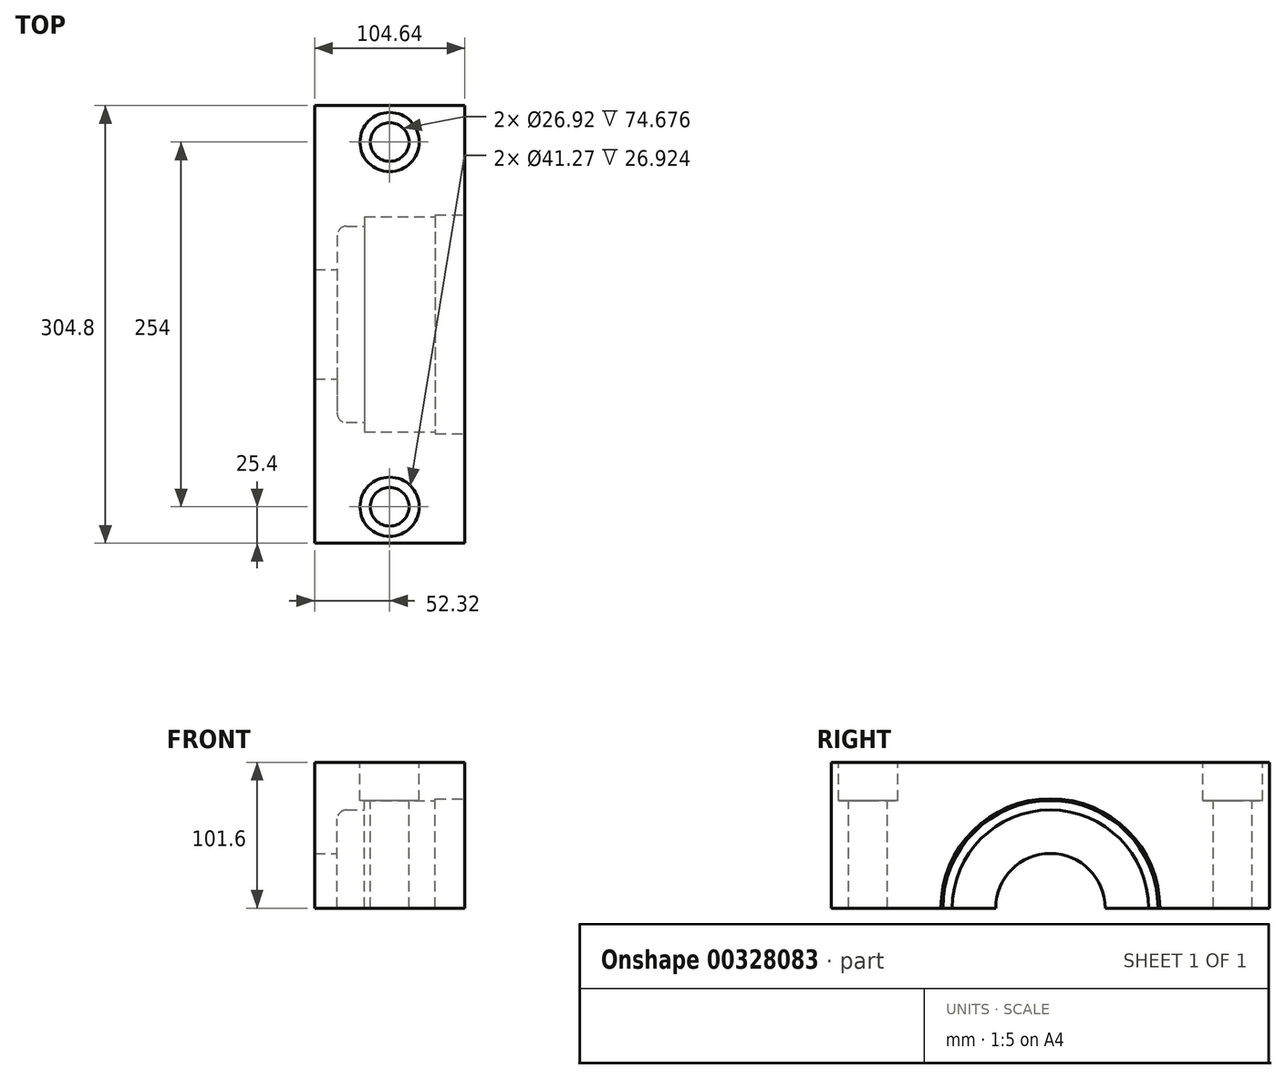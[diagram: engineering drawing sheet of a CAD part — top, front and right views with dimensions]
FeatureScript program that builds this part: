
annotation { "Feature Type Name" : "Feature", "Feature Type Description" : "" }
export const myFeature = defineFeature(function(context is Context, id is Id, definition is map)
    precondition{}
    {
        {
            var Q0;
            Q0=qCreatedBy(makeId("Right.planeOp"),FACE);
            var sketch = newSketch(context, id + "F0", { "sketchPlane" : qUnion([Q0])});
            skLineSegment(sketch, "E0.bottom", {"start": v(0, 0) * mm, "end": v(-152.4, 0) * mm});
            skLineSegment(sketch, "E0.top", {"start": v(0, 101.6) * mm, "end": v(-152.4, 101.6) * mm});
            skLineSegment(sketch, "E0.right", {"start": v(-152.4, 0) * mm, "end": v(-152.4, 101.6) * mm});
            skLineSegment(sketch, "E1.MirrorCS", {"start": v(0, 101.6) * mm, "end": v(152.4, 101.6) * mm});
            skLineSegment(sketch, "E2.MirrorCS", {"start": v(0, 0) * mm, "end": v(152.4, 0) * mm});
            skLineSegment(sketch, "E3.MirrorCS", {"start": v(152.4, 0) * mm, "end": v(152.4, 101.6) * mm});
            skSolve(sketch);
        }
        {
            var Q0;
            Q0 = qSketchRegion(id + "F0", true);
            extrude(context, id + "F1", {"entities" : qUnion([Q0]), "endBound" : BoundingType.SYMMETRIC, "depth" : 104.65 * mm});
        }
        {
            var Q0;
            Q0=makeQuery(id+"F1.opExtrude","CAP_FACE",FACE,{"disambiguationData":[OSD([sQuery(id+"F0.wireOp",EDGE,"E0.bottom"),sQuery(id+"F0.wireOp",EDGE,"E0.top"),sQuery(id+"F0.wireOp",EDGE,"E0.right"),sQuery(id+"F0.wireOp",EDGE,"E1.MirrorCS"),sQuery(id+"F0.wireOp",EDGE,"E2.MirrorCS"),sQuery(id+"F0.wireOp",EDGE,"E3.MirrorCS")])],"isStart":false});
            var sketch = newSketch(context, id + "F2", { "sketchPlane" : qUnion([Q0])});
            skCircle(sketch, "E4", {"center": v(0, 0) * mm, "radius": 38.1 * mm});
            skSolve(sketch);
        }
        {
            var Q0;
            Q0 = qSketchRegion(id + "F2", true);
            extrude(context, id + "F3", {"entities" : qUnion([Q0]), "operationType" : NewBodyOperationType.REMOVE, "endBound" : BoundingType.THROUGH_ALL, "oppositeDirection" : true, "depth" : 25.4 * mm});
        }
        {
            var Q0;
            Q0=makeQuery(id+"F1.opExtrude","CAP_FACE",FACE,{"disambiguationData":[OSD([sQuery(id+"F0.wireOp",EDGE,"E0.bottom"),sQuery(id+"F0.wireOp",EDGE,"E0.top"),sQuery(id+"F0.wireOp",EDGE,"E0.right"),sQuery(id+"F0.wireOp",EDGE,"E1.MirrorCS"),sQuery(id+"F0.wireOp",EDGE,"E2.MirrorCS"),sQuery(id+"F0.wireOp",EDGE,"E3.MirrorCS")])],"isStart":false});
            var sketch = newSketch(context, id + "F4", { "sketchPlane" : qUnion([Q0])});
            skCircle(sketch, "E5", {"center": v(0, 0) * mm, "radius": 68.33 * mm});
            skSolve(sketch);
        }
        {
            var Q0;
            Q0 = qSketchRegion(id + "F4", true);
            extrude(context, id + "F5", {"entities" : qUnion([Q0]), "operationType" : NewBodyOperationType.REMOVE, "oppositeDirection" : true, "depth" : 88.9 * mm});
        }
        {
            var Q0;
            Q0=makeQuery(id+"F5.boolean.opBoolean","COPY",EDGE,{"derivedFrom":makeQuery(id+"F5.opExtrude","CAP_EDGE",EDGE,{"disambiguationData":[OSD([sQuery(id+"F4.wireOp",EDGE,"E5")])],"isStart":false})});
            fillet(context, id + "F6", {"entities" : qUnion([Q0]), "radius" : 6.35 * mm, "tangentPropagation" : true, "allowEdgeOverflow" : false});
        }
        {
            var Q0;
            Q0=makeQuery(id+"F1.opExtrude","CAP_FACE",FACE,{"disambiguationData":[OSD([sQuery(id+"F0.wireOp",EDGE,"E0.bottom"),sQuery(id+"F0.wireOp",EDGE,"E0.top"),sQuery(id+"F0.wireOp",EDGE,"E0.right"),sQuery(id+"F0.wireOp",EDGE,"E1.MirrorCS"),sQuery(id+"F0.wireOp",EDGE,"E2.MirrorCS"),sQuery(id+"F0.wireOp",EDGE,"E3.MirrorCS")])],"isStart":false});
            var sketch = newSketch(context, id + "F7", { "sketchPlane" : qUnion([Q0])});
            skCircle(sketch, "E6", {"center": v(0, 0) * mm, "radius": 74.93 * mm});
            skSolve(sketch);
        }
        {
            var Q0;
            Q0 = qSketchRegion(id + "F7", true);
            extrude(context, id + "F8", {"entities" : qUnion([Q0]), "operationType" : NewBodyOperationType.REMOVE, "oppositeDirection" : true, "depth" : 69.85 * mm});
        }
        {
            var Q0;
            Q0=makeQuery(id+"F1.opExtrude","CAP_FACE",FACE,{"disambiguationData":[OSD([sQuery(id+"F0.wireOp",EDGE,"E0.bottom"),sQuery(id+"F0.wireOp",EDGE,"E0.top"),sQuery(id+"F0.wireOp",EDGE,"E0.right"),sQuery(id+"F0.wireOp",EDGE,"E1.MirrorCS"),sQuery(id+"F0.wireOp",EDGE,"E2.MirrorCS"),sQuery(id+"F0.wireOp",EDGE,"E3.MirrorCS")])],"isStart":false});
            var sketch = newSketch(context, id + "F9", { "sketchPlane" : qUnion([Q0])});
            skCircle(sketch, "E7", {"center": v(0, 0) * mm, "radius": 76.2 * mm});
            skSolve(sketch);
        }
        {
            var Q0;
            Q0 = qSketchRegion(id + "F9", true);
            extrude(context, id + "F10", {"entities" : qUnion([Q0]), "operationType" : NewBodyOperationType.REMOVE, "oppositeDirection" : true, "depth" : 20.57 * mm});
        }
        {
            var Q0;
            Q0=makeQuery(id+"F1.opExtrude","SWEPT_FACE",FACE,{"disambiguationData":[OSD([sQuery(id+"F0.wireOp",EDGE,"E0.top"),sQuery(id+"F0.wireOp",EDGE,"E1.MirrorCS")])]});
            var sketch = newSketch(context, id + "F11", { "sketchPlane" : qUnion([Q0])});
            skLineSegment(sketch, "E8.0", {"start": v(0, -152.4) * mm, "end": v(0, 152.4) * mm, "construction": true});
            skLineSegment(sketch, "E9", {"start": v(-98.53, 0) * mm, "end": v(104.23, 0) * mm, "construction": true});
            skLineSegment(sketch, "E10.0", {"start": v(-98.53, -127) * mm, "end": v(104.23, -127) * mm, "construction": true});
            skPoint(sketch, "E11", {"position": v(0, -127) * mm});
            skPoint(sketch, "E12.MirrorP", {"position": v(0, 127) * mm});
            skSolve(sketch);
        }
        {
            var Q0;
            Q0=sQuery(id+"F11.wireOp",VERTEX,"E11");
            var Q1;
            Q1=sQuery(id+"F11.wireOp",VERTEX,"E12.MirrorP");
            var Q2;
            Q2=makeQuery(id+"F1.opExtrude","SWEPT_BODY",BODY,{"disambiguationData":[OSD([sQuery(id+"F0.wireOp",EDGE,"E0.bottom"),sQuery(id+"F0.wireOp",EDGE,"E0.top"),sQuery(id+"F0.wireOp",EDGE,"E0.right"),sQuery(id+"F0.wireOp",EDGE,"E1.MirrorCS"),sQuery(id+"F0.wireOp",EDGE,"E2.MirrorCS"),sQuery(id+"F0.wireOp",EDGE,"E3.MirrorCS")])]});
            hole(context, id + "F12", {"style" : HoleStyle.C_BORE, "endStyle" : HoleEndStyle.THROUGH, "holeDiameter" : 26.92 * mm, "cBoreDiameter" : 41.27 * mm, "cBoreDepth" : 26.92 * mm, "tappedDepth" : 19.54 * mm, "tapClearance" : 3, "locations" : qUnion([Q0, Q1]), "scope" : qUnion([Q2])});
        }
    });
